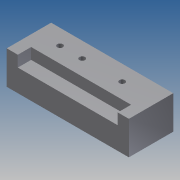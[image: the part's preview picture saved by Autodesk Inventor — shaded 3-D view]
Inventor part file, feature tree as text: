
AUTODESK INVENTOR PART (.ipt)
format: ipt  version: 2014 (Build 180170000, 170)  size: 129,536 bytes
history: native  units: mm
features: extrude x3
ambient origin geometry x8: Origin, YZ Plane, XZ Plane, XY Plane, X Axis, Y Axis, Z Axis, Center Point
bodies: Body1 (feature_tree)
feature tree (3):
  extrude  "Extrusion2"  Depth=1000.0mm
  extrude  "Extrusion3"  Depth=1000.0mm
  extrude  "Extrusion4"  Depth=60.0mm
